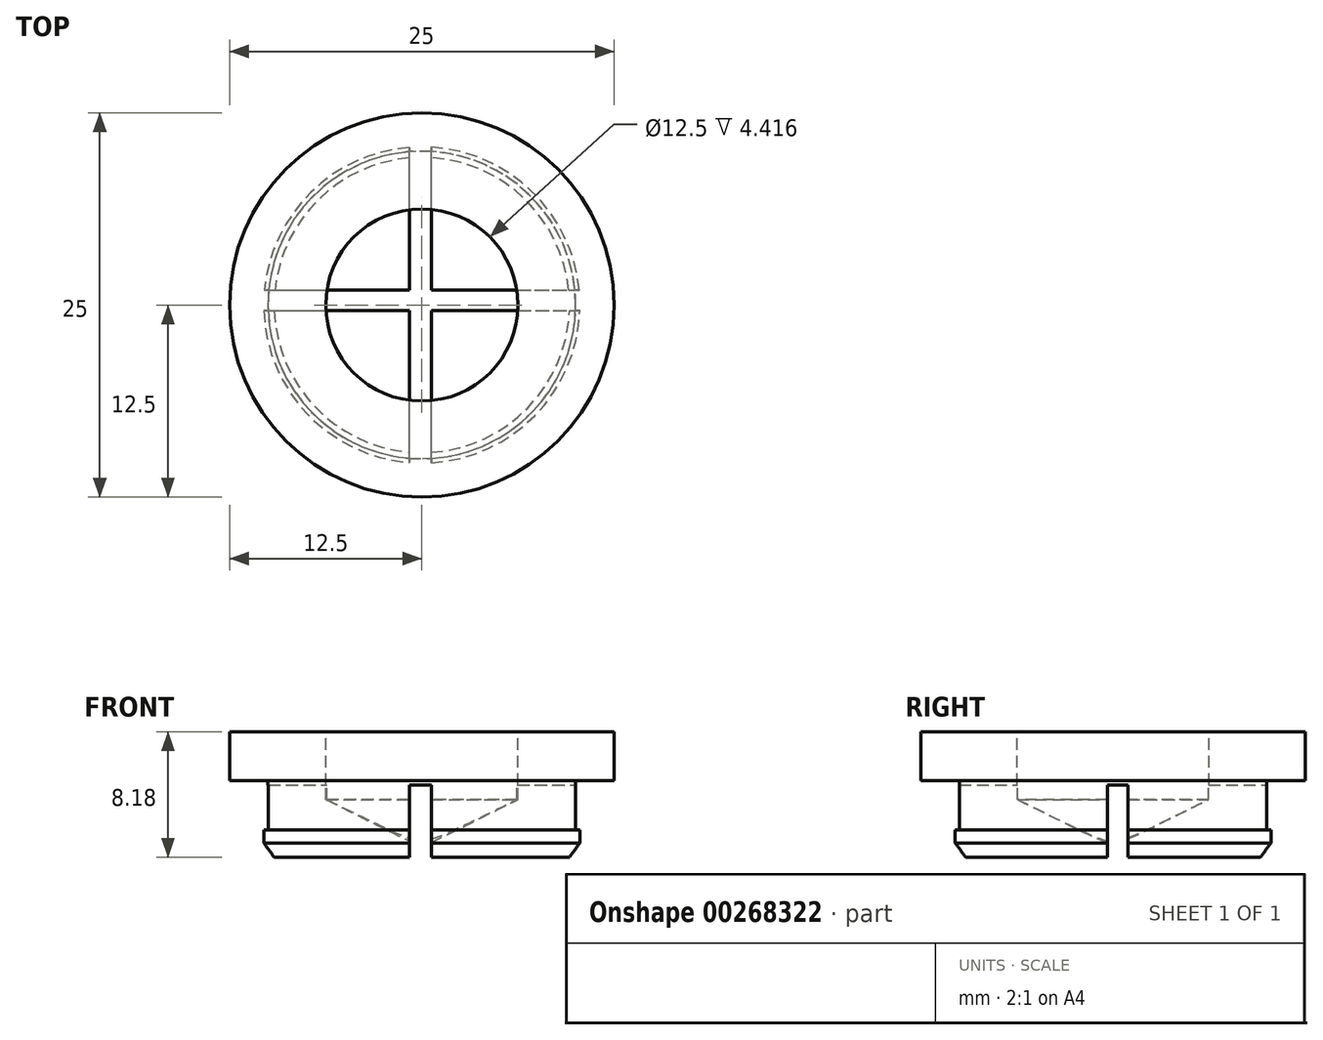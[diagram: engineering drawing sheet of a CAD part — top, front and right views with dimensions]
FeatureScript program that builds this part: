
annotation { "Feature Type Name" : "Feature", "Feature Type Description" : "" }
export const myFeature = defineFeature(function(context is Context, id is Id, definition is map)
    precondition{}
    {
        {
            var Q0;
            Q0=qCreatedBy(makeId("Front.planeOp"),FACE);
            var sketch = newSketch(context, id + "F0", { "sketchPlane" : qUnion([Q0])});
            skLineSegment(sketch, "E0", {"start": v(12.5, 0) * mm, "end": v(12.5, -3.18) * mm});
            skLineSegment(sketch, "E1", {"start": v(12.5, -3.18) * mm, "end": v(10, -3.18) * mm});
            skLineSegment(sketch, "E2", {"start": v(10, -3.18) * mm, "end": v(10, -6.38) * mm});
            skLineSegment(sketch, "E3", {"start": v(10, -6.38) * mm, "end": v(10.28, -6.38) * mm});
            skLineSegment(sketch, "E4", {"start": v(10.28, -6.38) * mm, "end": v(10.28, -7.24) * mm});
            skLineSegment(sketch, "E5", {"start": v(10.28, -7.24) * mm, "end": v(9.6, -8.18) * mm});
            skLineSegment(sketch, "E6", {"start": v(9.6, -8.18) * mm, "end": v(0, -8.18) * mm});
            skLineSegment(sketch, "E7", {"start": v(6.25, 0) * mm, "end": v(6.25, -4.42) * mm});
            skLineSegment(sketch, "E8", {"start": v(6.25, -4.42) * mm, "end": v(0, -7.55) * mm});
            skLineSegment(sketch, "E9", {"start": v(0, -7.55) * mm, "end": v(0, -8.18) * mm});
            skLineSegment(sketch, "E10", {"start": v(6.25, 0) * mm, "end": v(12.5, 0) * mm});
            skSolve(sketch);
        }
        {
            var Q0;
            Q0=makeQuery(id+"F0.imprint","IMPRINT",FACE,{"disambiguationData":[TD([[makeQuery(id+"F0.imprint","IMPRINT",EDGE,{"derivedFrom":sQuery(id+"F0.wireOp",EDGE,"E0")}),-1.0]])]});
            var Q1;
            Q1=sQuery(id+"F0.wireOp",EDGE,"E9");
            revolve(context, id + "F1", {"entities" : qUnion([Q0]), "axis" : qUnion([Q1]), "revolveType" : RevolveType.FULL});
        }
        {
            var Q0;
            Q0=makeQuery(id+"F1.opRevolve","SWEPT_FACE",FACE,{"disambiguationData":[OSD([sQuery(id+"F0.wireOp",EDGE,"E6")])]});
            var sketch = newSketch(context, id + "F2", { "sketchPlane" : qUnion([Q0])});
            skLineSegment(sketch, "E11.bottom", {"start": v(-0.82, 10.64) * mm, "end": v(0.61, 10.64) * mm});
            skLineSegment(sketch, "E11.top", {"start": v(-0.82, -11.44) * mm, "end": v(0.61, -11.44) * mm});
            skLineSegment(sketch, "E11.left", {"start": v(-0.82, 10.64) * mm, "end": v(-0.82, -11.44) * mm});
            skLineSegment(sketch, "E11.right", {"start": v(0.61, 10.64) * mm, "end": v(0.61, -11.44) * mm});
            skLineSegment(sketch, "E12.bottom", {"start": v(-10.68, 0.36) * mm, "end": v(11, 0.36) * mm});
            skLineSegment(sketch, "E12.top", {"start": v(-10.68, -0.97) * mm, "end": v(11, -0.97) * mm});
            skLineSegment(sketch, "E12.left", {"start": v(-10.68, 0.36) * mm, "end": v(-10.68, -0.97) * mm});
            skLineSegment(sketch, "E12.right", {"start": v(11, 0.36) * mm, "end": v(11, -0.97) * mm});
            skSolve(sketch);
        }
        {
            var Q0;
            Q0=qSketchRegion(id+"F2",true);
            extrude(context, id + "F3", {"entities" : qUnion([Q0]), "operationType" : NewBodyOperationType.REMOVE, "oppositeDirection" : true, "depth" : 4.7 * mm});
        }
    });
